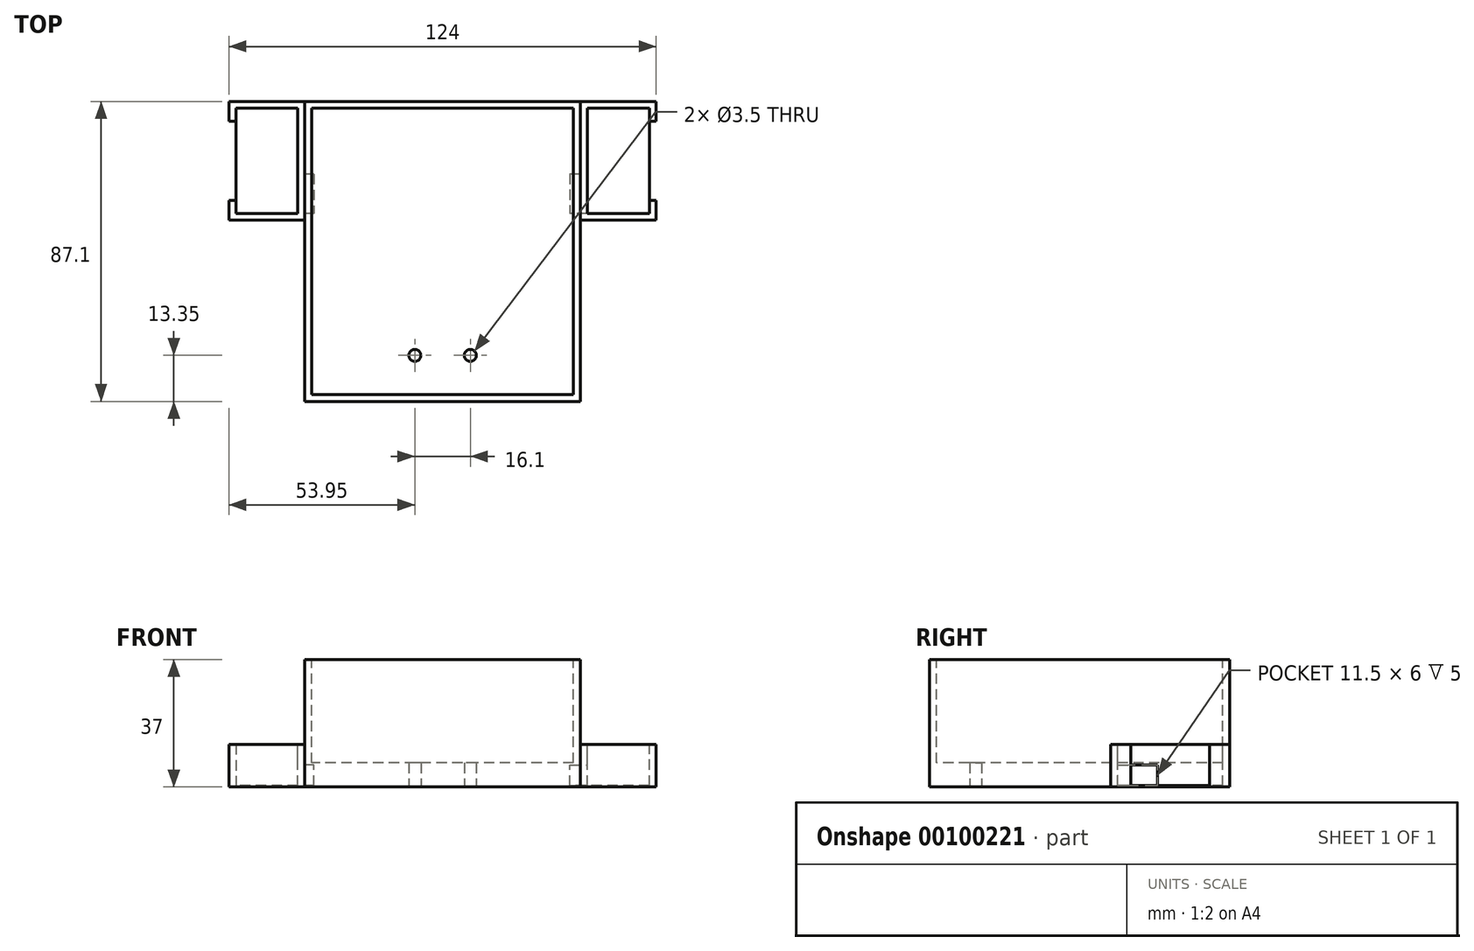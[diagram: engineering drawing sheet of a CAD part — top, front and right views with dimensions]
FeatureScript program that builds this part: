
annotation { "Feature Type Name" : "Feature", "Feature Type Description" : "" }
export const myFeature = defineFeature(function(context is Context, id is Id, definition is map)
    precondition{}
    {
        {
            var Q0;
            Q0=qCreatedBy(makeId("Top.planeOp"),FACE);
            var sketch = newSketch(context, id + "F0", { "sketchPlane" : qUnion([Q0])});
            skLineSegment(sketch, "E0.bottom", {"start": v(40, 43.55) * mm, "end": v(-40, 43.55) * mm});
            skLineSegment(sketch, "E0.top", {"start": v(40, -43.55) * mm, "end": v(-40, -43.55) * mm});
            skLineSegment(sketch, "E0.left", {"start": v(40, 43.55) * mm, "end": v(40, -43.55) * mm});
            skLineSegment(sketch, "E0.right", {"start": v(-40, 43.55) * mm, "end": v(-40, -43.55) * mm});
            skPoint(sketch, "E0.middle", {"position": v(0, 0) * mm});
            skSolve(sketch);
        }
        {
            var Q0;
            Q0=makeQuery(id+"F0.imprint","IMPRINT",FACE,{"disambiguationData":[TD([[makeQuery(id+"F0.imprint","IMPRINT",EDGE,{"derivedFrom":sQuery(id+"F0.wireOp",EDGE,"E0.bottom")}),1.0]])]});
            extrude(context, id + "F1", {"entities" : qUnion([Q0]), "depth" : 37 * mm});
        }
        {
            var Q0;
            Q0=makeQuery(id+"F1.opExtrude","CAP_FACE",FACE,{"disambiguationData":[OSD([sQuery(id+"F0.wireOp",EDGE,"E0.bottom"),sQuery(id+"F0.wireOp",EDGE,"E0.top"),sQuery(id+"F0.wireOp",EDGE,"E0.left"),sQuery(id+"F0.wireOp",EDGE,"E0.right")])],"isStart":false});
            var sketch = newSketch(context, id + "F2", { "sketchPlane" : qUnion([Q0])});
            skLineSegment(sketch, "E1.bottom", {"start": v(38, 41.55) * mm, "end": v(-38, 41.55) * mm});
            skLineSegment(sketch, "E1.top", {"start": v(38, -41.55) * mm, "end": v(-38, -41.55) * mm});
            skLineSegment(sketch, "E1.left", {"start": v(38, 41.55) * mm, "end": v(38, -41.55) * mm});
            skLineSegment(sketch, "E1.right", {"start": v(-38, 41.55) * mm, "end": v(-38, -41.55) * mm});
            skPoint(sketch, "E1.middle", {"position": v(0, 0) * mm});
            skSolve(sketch);
        }
        {
            var Q0;
            Q0=makeQuery(id+"F2.imprint","IMPRINT",FACE,{"disambiguationData":[TD([[makeQuery(id+"F2.imprint","IMPRINT",EDGE,{"derivedFrom":sQuery(id+"F2.wireOp",EDGE,"E1.bottom")}),1.0]])]});
            extrude(context, id + "F3", {"entities" : qUnion([Q0]), "operationType" : NewBodyOperationType.REMOVE, "oppositeDirection" : true, "depth" : 30 * mm});
        }
        {
            var Q0;
            Q0=makeQuery(id+"F1.opExtrude","CAP_FACE",FACE,{"disambiguationData":[OSD([sQuery(id+"F0.wireOp",EDGE,"E0.bottom"),sQuery(id+"F0.wireOp",EDGE,"E0.top"),sQuery(id+"F0.wireOp",EDGE,"E0.left"),sQuery(id+"F0.wireOp",EDGE,"E0.right")])],"isStart":true});
            var sketch = newSketch(context, id + "F4", { "sketchPlane" : qUnion([Q0])});
            skCircle(sketch, "E2", {"center": v(-8.05, 30.2) * mm, "radius": 1.75 * mm});
            skCircle(sketch, "E3.MirrorC", {"center": v(8.05, 30.2) * mm, "radius": 1.75 * mm});
            skSolve(sketch);
        }
        {
            var Q0;
            Q0=sQuery(id+"F4.wireOp",VERTEX,"E2.center");
            var Q1;
            Q1=sQuery(id+"F4.wireOp",VERTEX,"E3.MirrorC.center");
            var Q2;
            Q2=makeQuery(id+"F1.opExtrude","SWEPT_BODY",BODY,{"disambiguationData":[OSD([sQuery(id+"F0.wireOp",EDGE,"E0.bottom"),sQuery(id+"F0.wireOp",EDGE,"E0.top"),sQuery(id+"F0.wireOp",EDGE,"E0.left"),sQuery(id+"F0.wireOp",EDGE,"E0.right")])]});
            hole(context, id + "F5", {"style" : HoleStyle.SIMPLE, "endStyle" : HoleEndStyle.THROUGH, "holeDiameter" : 3.5 * mm, "locations" : qUnion([Q0, Q1]), "scope" : qUnion([Q2]), "isTappedThrough" : true});
        }
        {
            var Q0;
            Q0=makeQuery(id+"F1.opExtrude","SWEPT_FACE",FACE,{"disambiguationData":[OSD([sQuery(id+"F0.wireOp",EDGE,"E0.right")])]});
            var sketch = newSketch(context, id + "F6", { "sketchPlane" : qUnion([Q0])});
            skLineSegment(sketch, "E4.bottom", {"start": v(-43.55, 0) * mm, "end": v(-9.05, 0) * mm});
            skLineSegment(sketch, "E4.top", {"start": v(-43.55, 12.4) * mm, "end": v(-9.05, 12.4) * mm});
            skLineSegment(sketch, "E4.left", {"start": v(-43.55, 0) * mm, "end": v(-43.55, 12.4) * mm});
            skLineSegment(sketch, "E4.right", {"start": v(-9.05, 0) * mm, "end": v(-9.05, 12.4) * mm});
            skSolve(sketch);
        }
        {
            var Q0;
            Q0=makeQuery(id+"F6.imprint","IMPRINT",FACE,{"disambiguationData":[TD([[makeQuery(id+"F6.imprint","IMPRINT",EDGE,{"derivedFrom":sQuery(id+"F6.wireOp",EDGE,"E4.bottom")}),1.0]])]});
            extrude(context, id + "F7", {"entities" : qUnion([Q0]), "operationType" : NewBodyOperationType.ADD, "depth" : 22 * mm});
        }
        {
            var Q0;
            Q0=makeQuery(id+"F7.opExtrude","SWEPT_FACE",FACE,{"disambiguationData":[OSD([sQuery(id+"F6.wireOp",EDGE,"E4.top")])]});
            var sketch = newSketch(context, id + "F8", { "sketchPlane" : qUnion([Q0])});
            skLineSegment(sketch, "E5.bottom", {"start": v(-42, 41.55) * mm, "end": v(-60, 41.55) * mm});
            skLineSegment(sketch, "E5.top", {"start": v(-42, 11.05) * mm, "end": v(-60, 11.05) * mm});
            skLineSegment(sketch, "E5.left", {"start": v(-42, 41.55) * mm, "end": v(-42, 11.05) * mm});
            skLineSegment(sketch, "E5.right", {"start": v(-60, 41.55) * mm, "end": v(-60, 11.05) * mm});
            skPoint(sketch, "E5.middle", {"position": v(-51, 26.3) * mm});
            skSolve(sketch);
        }
        {
            var Q0;
            Q0 = qSketchRegion(id + "F8", true);
            extrude(context, id + "F9", {"entities" : qUnion([Q0]), "operationType" : NewBodyOperationType.REMOVE, "oppositeDirection" : true, "depth" : 12 * mm});
        }
        {
            var Q0;
            Q0=makeQuery(id+"F9.boolean.opBoolean","COPY",FACE,{"derivedFrom":makeQuery(id+"F9.opExtrude","SWEPT_FACE",FACE,{"disambiguationData":[OSD([sQuery(id+"F8.wireOp",EDGE,"E5.left")])]})});
            var sketch = newSketch(context, id + "F10", { "sketchPlane" : qUnion([Q0])});
            skPoint(sketch, "E6.oppositeSnap0", {"position": v(-11.05, 6.4) * mm});
            skLineSegment(sketch, "E6.bottom", {"start": v(-11.05, 0.4) * mm, "end": v(-22.47, 0.4) * mm});
            skLineSegment(sketch, "E6.top", {"start": v(-11.05, 6.4) * mm, "end": v(-22.47, 6.4) * mm});
            skLineSegment(sketch, "E6.left", {"start": v(-11.05, 0.4) * mm, "end": v(-11.05, 6.4) * mm});
            skLineSegment(sketch, "E6.right", {"start": v(-22.47, 0.4) * mm, "end": v(-22.47, 6.4) * mm});
            skSolve(sketch);
        }
        {
            var Q0;
            Q0=makeQuery(id+"F10.imprint","IMPRINT",FACE,{"disambiguationData":[TD([[makeQuery(id+"F10.imprint","IMPRINT",EDGE,{"derivedFrom":sQuery(id+"F10.wireOp",EDGE,"E6.bottom")}),1.0]])]});
            extrude(context, id + "F11", {"entities" : qUnion([Q0]), "operationType" : NewBodyOperationType.REMOVE, "oppositeDirection" : true, "depth" : 4.6 * mm});
        }
        {
            var Q0;
            Q0=makeQuery(id+"F1.opExtrude","SWEPT_FACE",FACE,{"disambiguationData":[OSD([sQuery(id+"F0.wireOp",EDGE,"E0.left")])]});
            var sketch = newSketch(context, id + "F12", { "sketchPlane" : qUnion([Q0])});
            skLineSegment(sketch, "E7.bottom", {"start": v(9.05, 0) * mm, "end": v(43.55, 0) * mm});
            skLineSegment(sketch, "E7.top", {"start": v(9.05, 12.4) * mm, "end": v(43.55, 12.4) * mm});
            skLineSegment(sketch, "E7.left", {"start": v(9.05, 0) * mm, "end": v(9.05, 12.4) * mm});
            skLineSegment(sketch, "E7.right", {"start": v(43.55, 0) * mm, "end": v(43.55, 12.4) * mm});
            skSolve(sketch);
        }
        {
            var Q0;
            Q0=makeQuery(id+"F12.imprint","IMPRINT",FACE,{"disambiguationData":[TD([[makeQuery(id+"F12.imprint","IMPRINT",EDGE,{"derivedFrom":sQuery(id+"F12.wireOp",EDGE,"E7.bottom")}),-1.0]])]});
            extrude(context, id + "F13", {"entities" : qUnion([Q0]), "operationType" : NewBodyOperationType.ADD, "depth" : 22 * mm});
        }
        {
            var Q0;
            Q0=makeQuery(id+"F13.opExtrude","SWEPT_FACE",FACE,{"disambiguationData":[OSD([sQuery(id+"F12.wireOp",EDGE,"E7.top")])]});
            var sketch = newSketch(context, id + "F14", { "sketchPlane" : qUnion([Q0])});
            skLineSegment(sketch, "E8.bottom", {"start": v(60, 41.55) * mm, "end": v(42, 41.55) * mm});
            skLineSegment(sketch, "E8.top", {"start": v(60, 11.05) * mm, "end": v(42, 11.05) * mm});
            skLineSegment(sketch, "E8.left", {"start": v(60, 41.55) * mm, "end": v(60, 11.05) * mm});
            skLineSegment(sketch, "E8.right", {"start": v(42, 41.55) * mm, "end": v(42, 11.05) * mm});
            skPoint(sketch, "E8.middle", {"position": v(51, 26.3) * mm});
            skSolve(sketch);
        }
        {
            var Q0;
            Q0=makeQuery(id+"F14.imprint","IMPRINT",FACE,{"disambiguationData":[TD([[makeQuery(id+"F14.imprint","IMPRINT",EDGE,{"derivedFrom":sQuery(id+"F14.wireOp",EDGE,"E8.bottom")}),1.0]])]});
            extrude(context, id + "F15", {"entities" : qUnion([Q0]), "operationType" : NewBodyOperationType.REMOVE, "oppositeDirection" : true, "depth" : 12 * mm});
        }
        {
            var Q0;
            Q0=makeQuery(id+"F15.boolean.opBoolean","COPY",FACE,{"derivedFrom":makeQuery(id+"F15.opExtrude","SWEPT_FACE",FACE,{"disambiguationData":[OSD([sQuery(id+"F14.wireOp",EDGE,"E8.right")])]})});
            var sketch = newSketch(context, id + "F16", { "sketchPlane" : qUnion([Q0])});
            skLineSegment(sketch, "E9.bottom", {"start": v(11.05, 0.4) * mm, "end": v(22.55, 0.4) * mm});
            skLineSegment(sketch, "E9.top", {"start": v(11.05, 6.4) * mm, "end": v(22.55, 6.4) * mm});
            skLineSegment(sketch, "E9.left", {"start": v(11.05, 0.4) * mm, "end": v(11.05, 6.4) * mm});
            skLineSegment(sketch, "E9.right", {"start": v(22.55, 0.4) * mm, "end": v(22.55, 6.4) * mm});
            skSolve(sketch);
        }
        {
            var Q0;
            Q0=makeQuery(id+"F16.imprint","IMPRINT",FACE,{"disambiguationData":[TD([[makeQuery(id+"F16.imprint","IMPRINT",EDGE,{"derivedFrom":sQuery(id+"F16.wireOp",EDGE,"E9.bottom")}),-1.0]])]});
            extrude(context, id + "F17", {"entities" : qUnion([Q0]), "operationType" : NewBodyOperationType.REMOVE, "oppositeDirection" : true, "depth" : 5 * mm});
        }
        {
            var Q0;
            Q0=makeQuery(id+"F13.opExtrude","CAP_FACE",FACE,{"disambiguationData":[OSD([sQuery(id+"F12.wireOp",EDGE,"E7.bottom"),sQuery(id+"F12.wireOp",EDGE,"E7.top"),sQuery(id+"F12.wireOp",EDGE,"E7.left"),sQuery(id+"F12.wireOp",EDGE,"E7.right")])],"isStart":false});
            var sketch = newSketch(context, id + "F18", { "sketchPlane" : qUnion([Q0])});
            skPoint(sketch, "E10.startSnap0", {"position": v(26.3, 12.4) * mm});
            skLineSegment(sketch, "E11.bottom", {"start": v(37.75, 0) * mm, "end": v(14.85, 0) * mm});
            skLineSegment(sketch, "E11.top", {"start": v(37.75, 12.4) * mm, "end": v(14.85, 12.4) * mm});
            skLineSegment(sketch, "E11.left", {"start": v(37.75, 0) * mm, "end": v(37.75, 12.4) * mm});
            skLineSegment(sketch, "E11.right", {"start": v(14.85, 0) * mm, "end": v(14.85, 12.4) * mm});
            skPoint(sketch, "E11.middle", {"position": v(26.3, 6.2) * mm});
            skSolve(sketch);
        }
        {
            var Q0;
            Q0=makeQuery(id+"F7.opExtrude","CAP_FACE",FACE,{"disambiguationData":[OSD([sQuery(id+"F6.wireOp",EDGE,"E4.bottom"),sQuery(id+"F6.wireOp",EDGE,"E4.top"),sQuery(id+"F6.wireOp",EDGE,"E4.left"),sQuery(id+"F6.wireOp",EDGE,"E4.right")])],"isStart":false});
            var sketch = newSketch(context, id + "F19", { "sketchPlane" : qUnion([Q0])});
            skLineSegment(sketch, "E12.bottom", {"start": v(-14.85, 12.4) * mm, "end": v(-37.75, 12.4) * mm});
            skLineSegment(sketch, "E12.top", {"start": v(-14.85, 0) * mm, "end": v(-37.75, 0) * mm});
            skLineSegment(sketch, "E12.left", {"start": v(-14.85, 12.4) * mm, "end": v(-14.85, 0) * mm});
            skLineSegment(sketch, "E12.right", {"start": v(-37.75, 12.4) * mm, "end": v(-37.75, 0) * mm});
            skPoint(sketch, "E12.middle", {"position": v(-26.3, 6.2) * mm});
            skSolve(sketch);
        }
        {
            var Q0;
            Q0=makeQuery(id+"F19.imprint","IMPRINT",FACE,{"disambiguationData":[TD([[makeQuery(id+"F19.imprint","IMPRINT",EDGE,{"derivedFrom":sQuery(id+"F19.wireOp",EDGE,"E12.bottom")}),-1.0]])]});
            extrude(context, id + "F20", {"entities" : qUnion([Q0]), "operationType" : NewBodyOperationType.REMOVE, "oppositeDirection" : true, "depth" : 2 * mm});
        }
        {
            var Q0;
            Q0=makeQuery(id+"F18.imprint","IMPRINT",FACE,{"disambiguationData":[TD([[makeQuery(id+"F18.imprint","IMPRINT",EDGE,{"derivedFrom":sQuery(id+"F18.wireOp",EDGE,"E11.bottom")}),-1.0]])]});
            extrude(context, id + "F21", {"entities" : qUnion([Q0]), "operationType" : NewBodyOperationType.REMOVE, "oppositeDirection" : true, "depth" : 2 * mm});
        }
    });
